# Revit family: 595x595_START Panel Backlit UGR19 - Copy - Copy (3)
name_source: partatom
category: Lighting Fixtures
revit_build: Autodesk Revit 2017 (Build: 20190507_1515(x64)
units: mm (PartAtom-declared; Revit-internal decimal feet)

## family parameters
Cut with Voids When Loaded = No
Host = Face
Light Source = Yes
OmniClass Number = 23.80.70.00
OmniClass Title = Lighting
Part Type = Normal
Room Calculation Point = No
Round Connector Dimension = Use Diameter
Shared = No

## types (1)
- 0042232
    -LUMDEPTH_SYL = -277 mm
    Apparent Load = 36 VA
    Assembly Code = D5020200
    AssetType = Fixed
    BOX_WIDTH_SYL = 40 mm  [stored 0.131234 ft]
    ClassificationName = Uniclass2015
    ClassificationValue = EF_70_80
    Color Filter = 16777215
    Cost = 0 $
    DEPTH_SYL = 298 mm
    Default Elevation = 1219 mm
    Dimming Lamp Color Temperature Shift = <None>
    DocumentationLiterature = http://www.sylvania-lighting.com
    ElectricShockClassification = Class II
    Emit Shape Visible in Rendering = No
    Emit from Circle Diameter = 610 mm
    HEIGHTBOTT_SYL = 7 mm  [stored 0.0229659 ft]
    HEIGHT_SYL = 33 mm  [stored 0.108268 ft]
    IfcExportAs = IfcLightFixtureType
    IfcExportType = IfcLightFixtureType
    ImpactProtectionIndex = IK03
    IngressProtection = IP40/20
    Keynote = 16500
    LUMDEPTH_SYL = 277 mm
    LUMWIDTH_SYL = 277 mm
    Lamp = LED
    LampColourRenderingIndex = 80
    LampColourTemperature = 4000 K
    LampMacAdamStep = 6
    LampNominalLuminous = 4000 lm
    LampsType = LED
    LuminousEfficacy = 111 lm/W
    MAINHEIGHT_SYL = 63 mm
    Manufacturer = Feilo Sylvania
    ManufacturerName = Feilo Sylvania
    Material = aluminium,steel housing, other diffuser
    Material_1_SYL = <By Category>
    Material_2_SYL = <By Category>
    Material_3_SYL = <By Category>
    Material_4_SYL = <By Category>
    Model = START Panel 600x600 4000Lm 840 LILO
    ModelNumber = 0042232
    ModelReference = START Panel 600x600 4000Lm 840 LILO
    Name = START Panel 600x600 4000Lm 840 LILO
    NominalDepth = 595 mm
    NominalHeight = 35 mm
    NominalLength = 595 mm
    Photometric Web File = 0042232.ies
    PowerConsumption = 36 W
    PowerFactor = 0.9
    TOPWIDTH_SYL = 245 mm  [stored 0.803806 ft]
    Tilt Angle = -90.00°
    Type Image = <None>
    TypeName = 0042232 ST PANEL 600X600 4000LM 840 LILO
    URL = http://www.sylvania-lighting.com
    Voltage = 0 V
    WIDTH_SYL = 298 mm
    Weight = 119.34 kg

note: [stored X ft] marks values corroborated as IEEE doubles in the binary element streams (Revit-internal decimal feet)

## geometry (parser evidence)
native form markers: Sweep x2
no freeform markers — native parametric forms only
